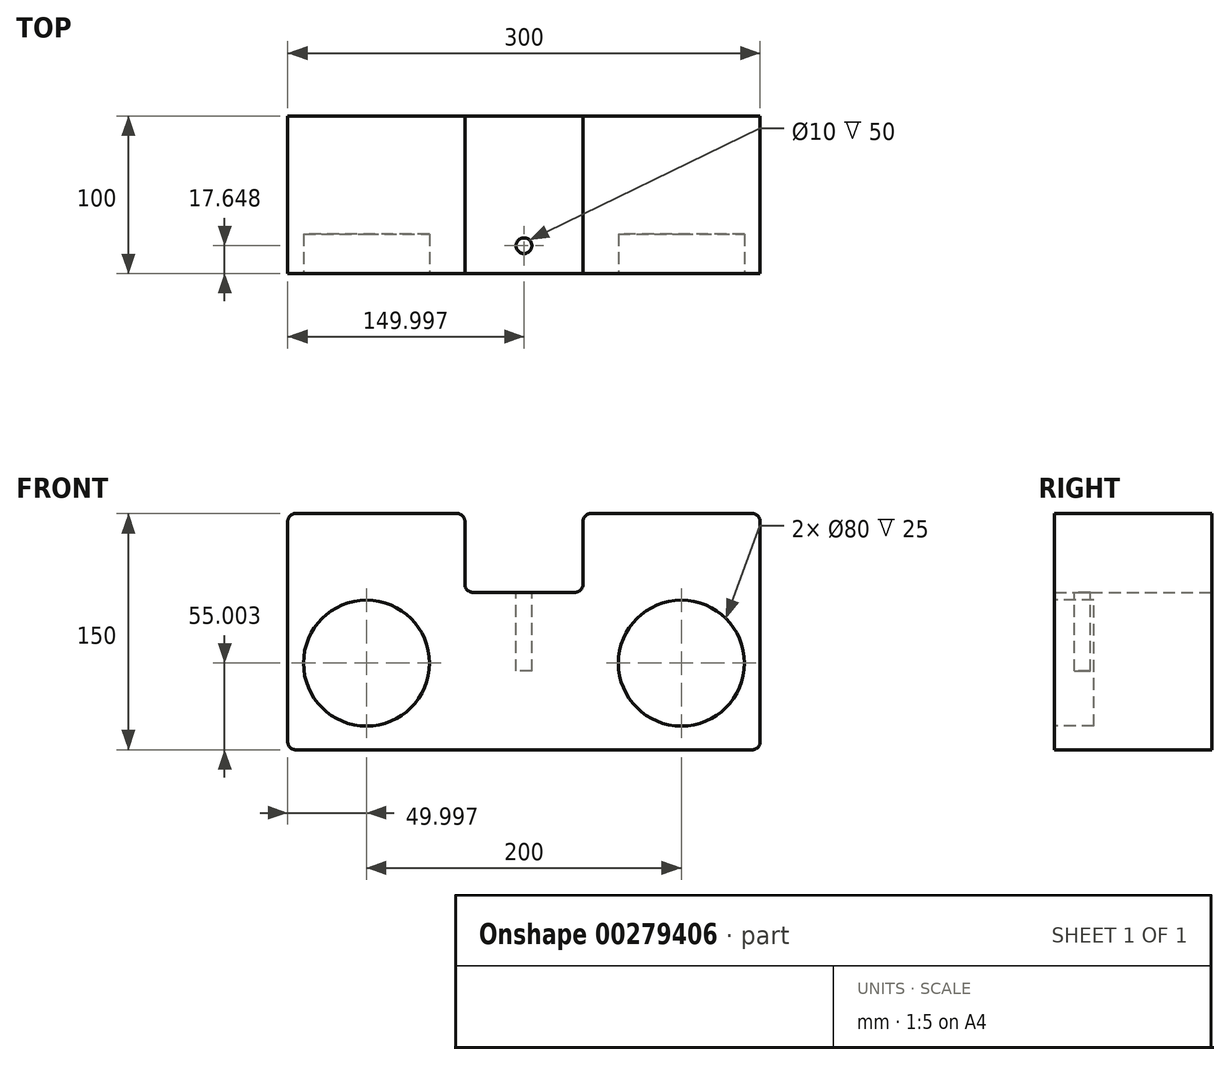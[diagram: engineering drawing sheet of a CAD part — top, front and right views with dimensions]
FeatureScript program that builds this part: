
annotation { "Feature Type Name" : "Feature", "Feature Type Description" : "" }
export const myFeature = defineFeature(function(context is Context, id is Id, definition is map)
    precondition{}
    {
        {
            var Q0;
            Q0=qCreatedBy(makeId("Front.planeOp"),FACE);
            var sketch = newSketch(context, id + "F0", { "sketchPlane" : qUnion([Q0])});
            skLineSegment(sketch, "E0", {"start": v(-160.55, 88.66) * mm, "end": v(-58.05, 88.66) * mm});
            skLineSegment(sketch, "E1", {"start": v(-53.05, 83.66) * mm, "end": v(-53.05, 43.66) * mm});
            skLineSegment(sketch, "E2", {"start": v(-48.05, 38.66) * mm, "end": v(16.95, 38.66) * mm});
            skLineSegment(sketch, "E3", {"start": v(21.95, 43.66) * mm, "end": v(21.95, 83.66) * mm});
            skLineSegment(sketch, "E4", {"start": v(26.95, 88.66) * mm, "end": v(129.45, 88.66) * mm});
            skLineSegment(sketch, "E5", {"start": v(134.45, 83.66) * mm, "end": v(134.45, -56.34) * mm});
            skLineSegment(sketch, "E6", {"start": v(129.45, -61.34) * mm, "end": v(-160.55, -61.34) * mm});
            skLineSegment(sketch, "E7", {"start": v(-165.55, -56.34) * mm, "end": v(-165.55, 83.66) * mm});
            skPoint(sketch, "E8.visualSharp", {"position": v(-165.55, 88.66) * mm});
            skArc(sketch, "E8.filletArc", {"start": v(-160.55, 88.66) * mm, "mid": v(-164.09, 87.2) * mm, "end": v(-165.55, 83.66) * mm});
            skPoint(sketch, "E9.visualSharp", {"position": v(-165.55, -61.34) * mm});
            skArc(sketch, "E9.filletArc", {"start": v(-165.55, -56.34) * mm, "mid": v(-164.09, -59.87) * mm, "end": v(-160.55, -61.34) * mm});
            skPoint(sketch, "E10.visualSharp", {"position": v(134.45, 88.66) * mm});
            skArc(sketch, "E10.filletArc", {"start": v(134.45, 83.66) * mm, "mid": v(132.98, 87.2) * mm, "end": v(129.45, 88.66) * mm});
            skPoint(sketch, "E11.visualSharp", {"position": v(134.45, -61.34) * mm});
            skArc(sketch, "E11.filletArc", {"start": v(129.45, -61.34) * mm, "mid": v(132.98, -59.87) * mm, "end": v(134.45, -56.34) * mm});
            skPoint(sketch, "E12.visualSharp", {"position": v(-53.05, 88.66) * mm});
            skArc(sketch, "E12.filletArc", {"start": v(-53.05, 83.66) * mm, "mid": v(-54.52, 87.2) * mm, "end": v(-58.05, 88.66) * mm});
            skPoint(sketch, "E13.visualSharp", {"position": v(21.95, 88.66) * mm});
            skArc(sketch, "E13.filletArc", {"start": v(26.95, 88.66) * mm, "mid": v(23.41, 87.2) * mm, "end": v(21.95, 83.66) * mm});
            skPoint(sketch, "E14.visualSharp", {"position": v(-53.05, 38.66) * mm});
            skArc(sketch, "E14.filletArc", {"start": v(-53.05, 43.66) * mm, "mid": v(-51.59, 40.13) * mm, "end": v(-48.05, 38.66) * mm});
            skPoint(sketch, "E15.visualSharp", {"position": v(21.95, 38.66) * mm});
            skArc(sketch, "E15.filletArc", {"start": v(16.95, 38.66) * mm, "mid": v(20.48, 40.13) * mm, "end": v(21.95, 43.66) * mm});
            skSolve(sketch);
        }
        {
            var Q0;
            Q0=makeQuery(id+"F0.imprint","IMPRINT",FACE,{"disambiguationData":[TD([[makeQuery(id+"F0.imprint","IMPRINT",EDGE,{"derivedFrom":sQuery(id+"F0.wireOp",EDGE,"E0")}),-1.0]])]});
            extrude(context, id + "F1", {"entities" : qUnion([Q0]), "depth" : 100 * mm});
        }
        {
            var Q0;
            Q0=makeQuery(id+"F1.opExtrude","CAP_FACE",FACE,{"disambiguationData":[OSD([sQuery(id+"F0.wireOp",EDGE,"E0"),sQuery(id+"F0.wireOp",EDGE,"E1"),sQuery(id+"F0.wireOp",EDGE,"E2"),sQuery(id+"F0.wireOp",EDGE,"E3"),sQuery(id+"F0.wireOp",EDGE,"E4"),sQuery(id+"F0.wireOp",EDGE,"E5"),sQuery(id+"F0.wireOp",EDGE,"E6"),sQuery(id+"F0.wireOp",EDGE,"E7"),sQuery(id+"F0.wireOp",EDGE,"E8.filletArc"),sQuery(id+"F0.wireOp",EDGE,"E9.filletArc"),sQuery(id+"F0.wireOp",EDGE,"E10.filletArc"),sQuery(id+"F0.wireOp",EDGE,"E11.filletArc"),sQuery(id+"F0.wireOp",EDGE,"E12.filletArc"),sQuery(id+"F0.wireOp",EDGE,"E13.filletArc"),sQuery(id+"F0.wireOp",EDGE,"E15.filletArc"),sQuery(id+"F0.wireOp",EDGE,"E14.filletArc")])],"isStart":false});
            var sketch = newSketch(context, id + "F2", { "sketchPlane" : qUnion([Q0])});
            skCircle(sketch, "E16", {"center": v(-115.55, -6.34) * mm, "radius": 40 * mm});
            skCircle(sketch, "E17", {"center": v(84.45, -6.34) * mm, "radius": 40 * mm});
            skSolve(sketch);
        }
        {
            var Q0;
            Q0 = qSketchRegion(id + "F2", true);
            extrude(context, id + "F3", {"entities" : qUnion([Q0]), "operationType" : NewBodyOperationType.REMOVE, "oppositeDirection" : true, "depth" : 25 * mm});
        }
        {
            var Q0;
            Q0=makeQuery(id+"F1.opExtrude","SWEPT_FACE",FACE,{"disambiguationData":[OSD([sQuery(id+"F0.wireOp",EDGE,"E2")])]});
            var sketch = newSketch(context, id + "F4", { "sketchPlane" : qUnion([Q0])});
            skCircle(sketch, "E18", {"center": v(-15.55, -82.35) * mm, "radius": 5 * mm});
            skSolve(sketch);
        }
        {
            var Q0;
            Q0 = qSketchRegion(id + "F4", true);
            extrude(context, id + "F5", {"entities" : qUnion([Q0]), "operationType" : NewBodyOperationType.REMOVE, "oppositeDirection" : true, "depth" : 50 * mm});
        }
    });
